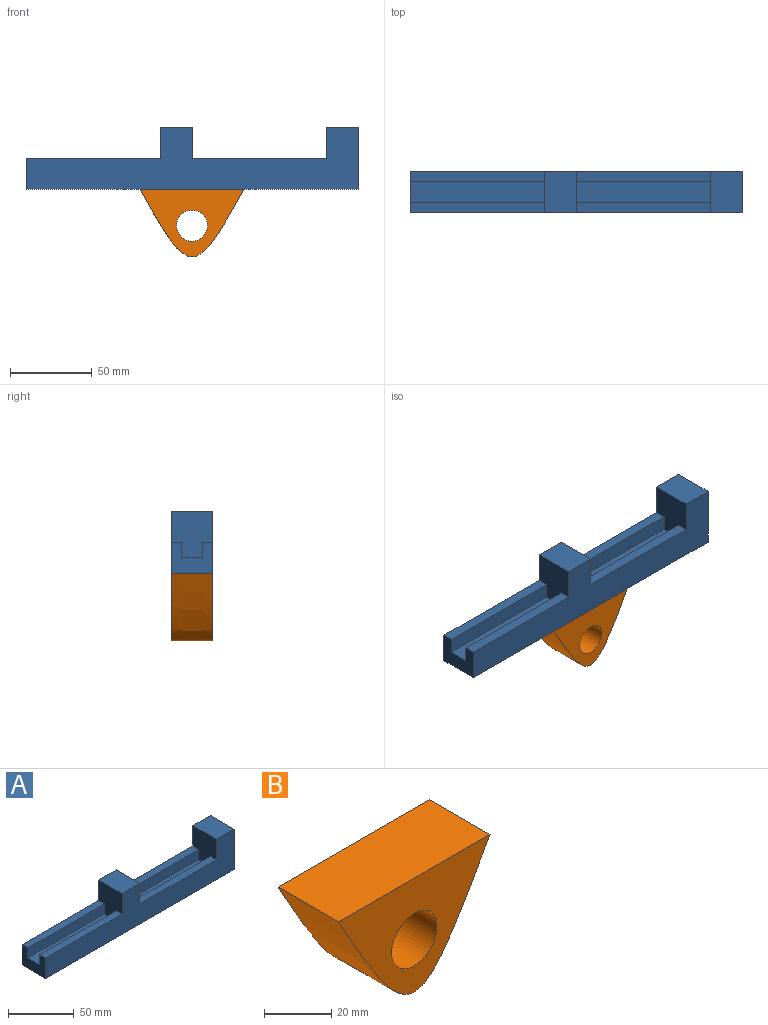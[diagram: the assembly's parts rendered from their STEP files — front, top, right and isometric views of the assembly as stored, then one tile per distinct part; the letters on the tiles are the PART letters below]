
ASSEMBLY  parts=2 mates=1
PART A: 20 faces, bbox 203.2x25.4x38.1 mm
  f0: plane 82.55x6.35mm, normal (0,0,1), area 524.2mm2, adj f5,f10,f12,f18
  f1: plane 82.55x6.35mm, normal (0,0,1), area 524.2mm2, adj f2,f5,f9,f15
  f2: plane 25.4x19.05mm, normal (-1,0,0), area 362.9mm2, adj f1,f4,f5,f7,f8,f14,f15,f16
  f3: plane 82.55x6.35mm, normal (0,0,1), area 524.2mm2, adj f4,f10,f12,f17
  f4: plane 203.2x38.1mm, normal (0,1,0), area 4596.8mm2, adj f2,f3,f6,f7,f8,f9,f10,f11
  f5: plane 203.2x38.1mm, normal (0,-1,0), area 4596.8mm2, adj f0,f1,f2,f6,f7,f9,f10,f11
  f6: plane 38.1x25.4mm, normal (1,0,0), area 967.7mm2, adj f4,f5,f7,f13
  f7: plane 203.2x25.4mm, normal (0,0,-1), area 5161.3mm2, adj f2,f4,f5,f6
  f8: plane 82.55x6.35mm, normal (0,0,1), area 524.2mm2, adj f2,f4,f9,f14
  f9: plane 28.58x25.4mm, normal (-1,0,0), area 604.8mm2, adj f1,f4,f5,f8,f11,f14,f15,f16
  f10: plane 28.58x25.4mm, normal (1,0,0), area 604.8mm2, adj f0,f3,f4,f5,f11,f17,f18,f19
  f11: plane 25.4x19.05mm, normal (0,0,1), area 483.9mm2, adj f4,f5,f9,f10
  f12: plane 28.58x25.4mm, normal (-1,0,0), area 604.8mm2, adj f0,f3,f4,f5,f13,f17,f18,f19
  f13: plane 25.4x19.05mm, normal (0,0,1), area 483.9mm2, adj f4,f5,f6,f12
  f14: plane 82.55x9.53mm, normal (0,-1,0), area 786.3mm2, adj f2,f8,f9,f16
  f15: plane 82.55x9.53mm, normal (0,1,0), area 786.3mm2, adj f1,f2,f9,f16
  f16: plane 82.55x12.7mm, normal (0,0,1), area 1048.4mm2, adj f2,f9,f14,f15
  f17: plane 82.55x9.53mm, normal (0,-1,0), area 786.3mm2, adj f3,f10,f12,f19
  f18: plane 82.55x9.53mm, normal (0,1,0), area 786.3mm2, adj f0,f10,f12,f19
  f19: plane 82.55x12.7mm, normal (0,0,1), area 1048.4mm2, adj f10,f12,f17,f18
PART B: 5 faces, bbox 63.5x25.4x42.3 mm
  f0: plane 63.5x25.4mm, normal (0,0,1), area 1612.9mm2, adj f1,f3,f4
  f1: extruded ~63.5x41.28mm, area 2715.7mm2, adj f0,f3,f4
  f2: cylinder r=9.53mm len=25.4mm, axis (0,1,0), area 1520.1mm2, adj f3,f4
  f3: plane 63.5x42.32mm, normal (0,-1,0), area 1311.8mm2, adj f0,f1,f2
  f4: plane 63.5x42.32mm, normal (0,1,0), area 1311.8mm2, adj f0,f1,f2
PLACE A at identity
PLACE B t=(45.26,25.4,-41.28)mm
MATE fastened B.f0 <-> A.f7  axis (0,0,1) through (45.26,12.7,-19.05)mm
